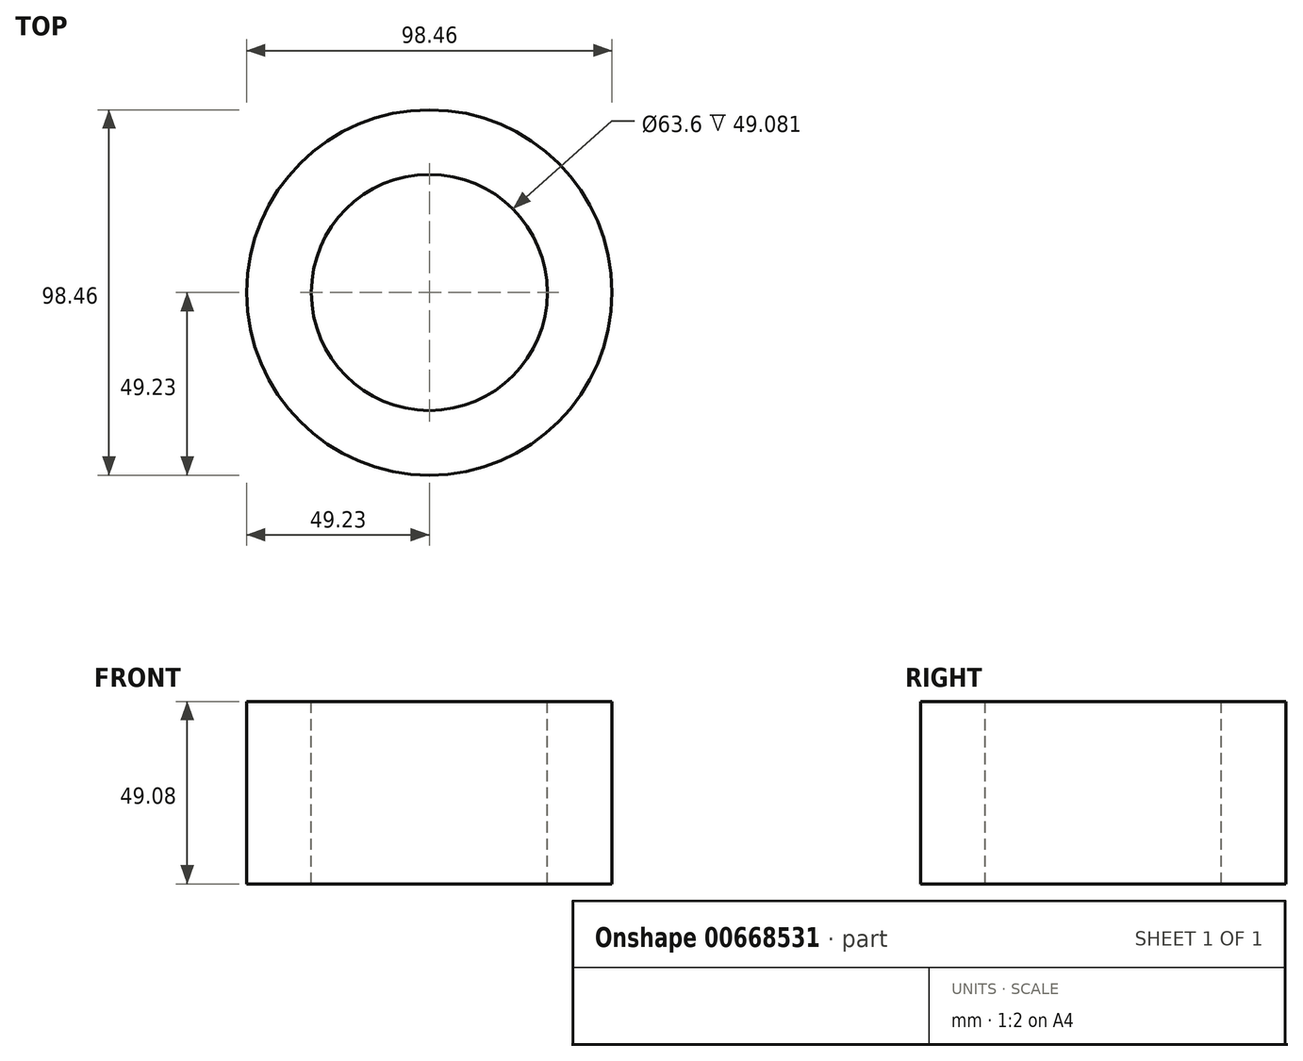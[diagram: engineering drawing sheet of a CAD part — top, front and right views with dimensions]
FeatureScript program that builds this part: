
annotation { "Feature Type Name" : "Feature", "Feature Type Description" : "" }
export const myFeature = defineFeature(function(context is Context, id is Id, definition is map)
    precondition{}
    {
        {
            var Q0;
            Q0=qCreatedBy(makeId("Front.planeOp"),FACE);
            var sketch = newSketch(context, id + "F0", { "sketchPlane" : qUnion([Q0])});
            skLineSegment(sketch, "E0", {"start": v(-49.23, 0) * mm, "end": v(-49.23, 49.08) * mm});
            skLineSegment(sketch, "E1", {"start": v(-49.23, 49.08) * mm, "end": v(-31.8, 49.08) * mm});
            skLineSegment(sketch, "E2", {"start": v(-31.8, 49.08) * mm, "end": v(-31.8, 0) * mm});
            skLineSegment(sketch, "E3", {"start": v(-31.8, 0) * mm, "end": v(-49.23, 0) * mm});
            skSolve(sketch);
        }
        {
            var Q0;
            Q0=qCreatedBy(makeId("Front.planeOp"),FACE);
            var sketch = newSketch(context, id + "F1", { "sketchPlane" : qUnion([Q0])});
            skLineSegment(sketch, "E4", {"start": v(0, 64.76) * mm, "end": v(0, -59.54) * mm, "construction": true});
            skSolve(sketch);
        }
        {
            var Q0;
            Q0 = qSketchRegion(id + "F1", true);
            var Q1;
            Q1=makeQuery(id+"F0.imprint","IMPRINT",FACE,{"disambiguationData":[TD([[makeQuery(id+"F0.imprint","IMPRINT",EDGE,{"derivedFrom":sQuery(id+"F0.wireOp",EDGE,"E0")}),-1.0]])]});
            var Q2;
            Q2=sQuery(id+"F1.wireOp",EDGE,"E4");
            revolve(context, id + "F2", {"entities" : qUnion([Q0, Q1]), "axis" : qUnion([Q2]), "revolveType" : RevolveType.FULL});
        }
    });
